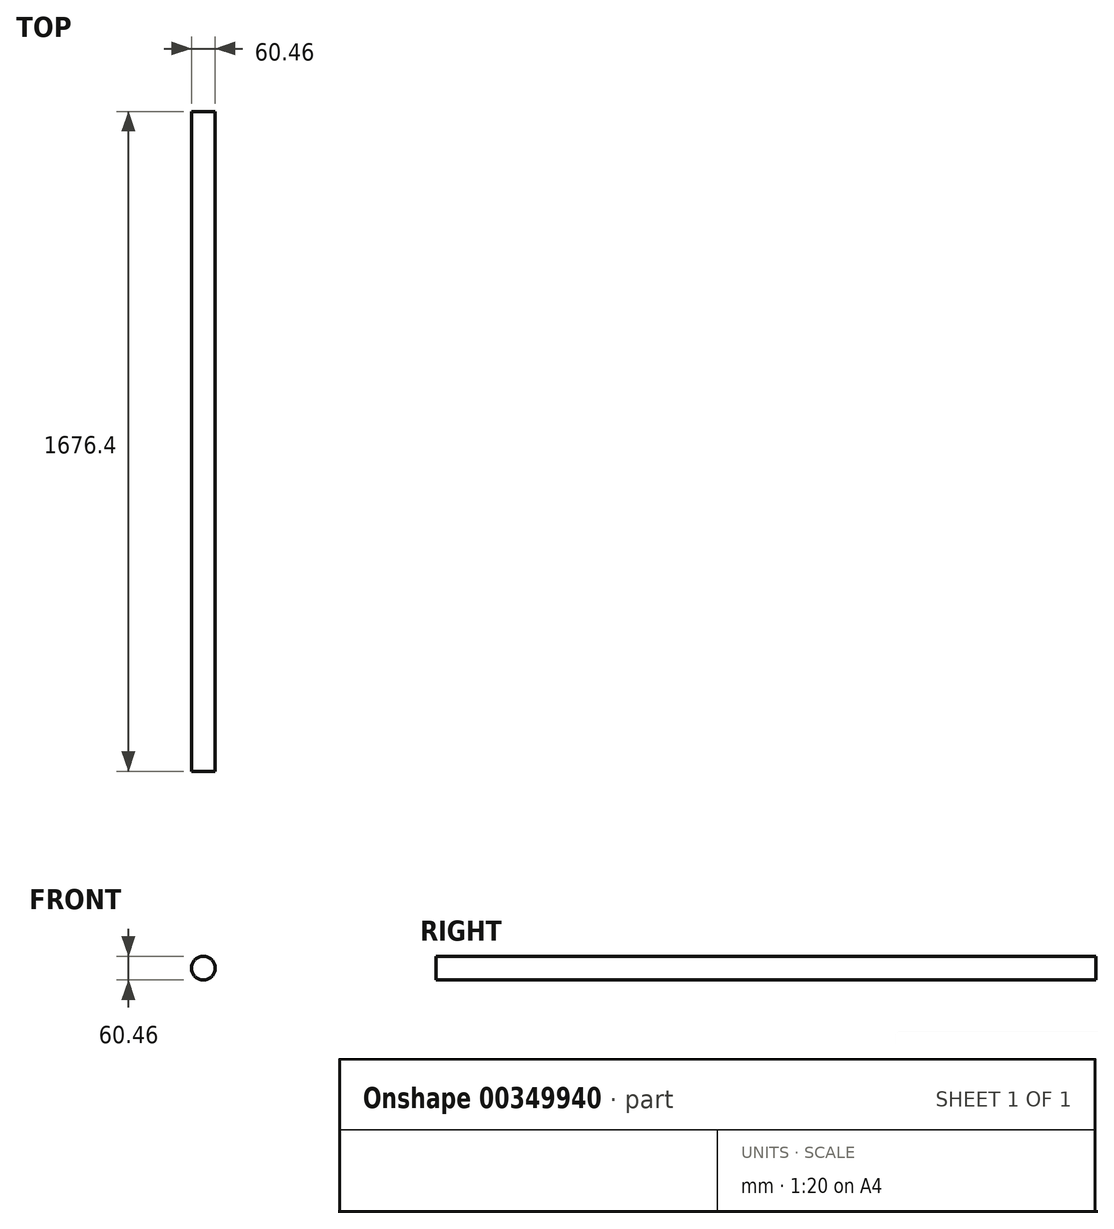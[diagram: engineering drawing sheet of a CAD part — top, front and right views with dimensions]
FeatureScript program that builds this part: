
annotation { "Feature Type Name" : "Feature", "Feature Type Description" : "" }
export const myFeature = defineFeature(function(context is Context, id is Id, definition is map)
    precondition{}
    {
        {
            var Q0;
            Q0=qCreatedBy(makeId("Front.planeOp"),FACE);
            var sketch = newSketch(context, id + "F0", { "sketchPlane" : qUnion([Q0])});
            skCircle(sketch, "E0", {"center": v(0, 0) * mm, "radius": 30.23 * mm});
            skSolve(sketch);
        }
        {
            var Q0;
            Q0 = qSketchRegion(id + "F0", true);
            extrude(context, id + "F1", {"entities" : qUnion([Q0]), "depth" : 1676.4 * mm, "offsetDistance" : 25.4 * mm});
        }
    });
